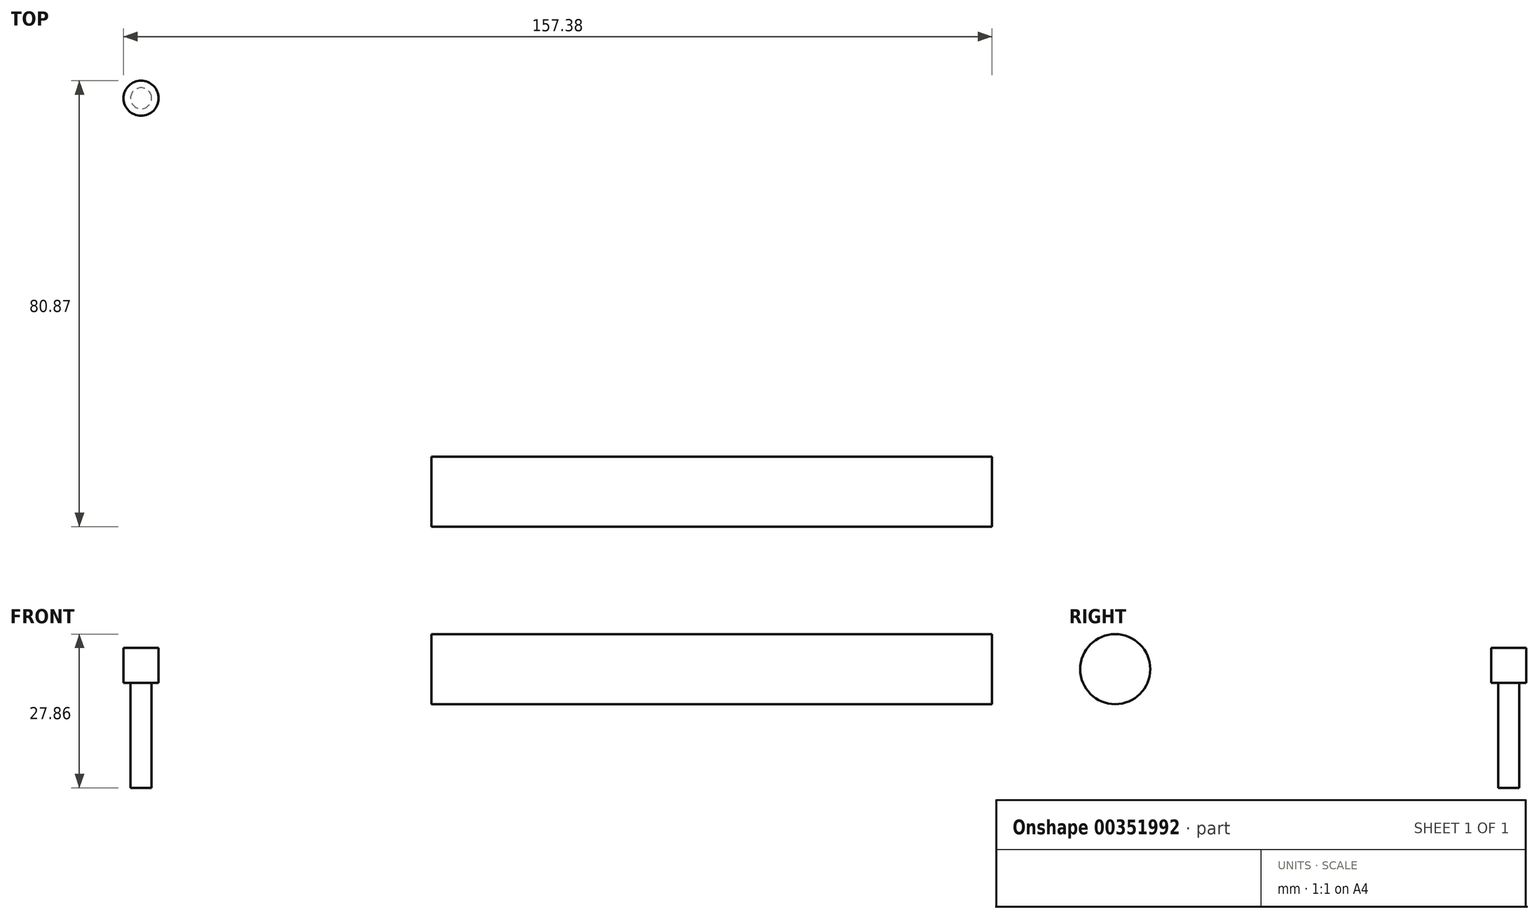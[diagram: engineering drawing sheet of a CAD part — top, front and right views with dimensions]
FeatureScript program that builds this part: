
annotation { "Feature Type Name" : "Feature", "Feature Type Description" : "" }
export const myFeature = defineFeature(function(context is Context, id is Id, definition is map)
    precondition{}
    {
        {
            var Q0;
            Q0=qCreatedBy(makeId("Right.planeOp"),FACE);
            var sketch = newSketch(context, id + "F0", { "sketchPlane" : qUnion([Q0])});
            skCircle(sketch, "E0", {"center": v(-34.98, 21.51) * mm, "radius": 6.35 * mm});
            skSolve(sketch);
        }
        {
            var Q0;
            Q0=makeQuery(id+"F0.imprint","IMPRINT",FACE,{"disambiguationData":[TD([[makeQuery(id+"F0.imprint","IMPRINT",EDGE,{"derivedFrom":sQuery(id+"F0.wireOp",EDGE,"E0")}),1.0]])]});
            extrude(context, id + "F1", {"entities" : qUnion([Q0]), "depth" : 101.6 * mm});
        }
        {
            var Q0;
            Q0=qCreatedBy(makeId("Top.planeOp"),FACE);
            var sketch = newSketch(context, id + "F2", { "sketchPlane" : qUnion([Q0])});
            skCircle(sketch, "E1", {"center": v(-52.6, 36.37) * mm, "radius": 1.9 * mm});
            skSolve(sketch);
        }
        {
            var Q0;
            Q0=makeQuery(id+"F2.imprint","IMPRINT",FACE,{"disambiguationData":[TD([[makeQuery(id+"F2.imprint","IMPRINT",EDGE,{"derivedFrom":sQuery(id+"F2.wireOp",EDGE,"E1")}),1.0]])]});
            extrude(context, id + "F3", {"entities" : qUnion([Q0]), "depth" : 19.05 * mm});
        }
        {
            var Q0;
            Q0=makeQuery(id+"F3.opExtrude","CAP_FACE",FACE,{"disambiguationData":[OSD([sQuery(id+"F2.wireOp",EDGE,"E1")])],"isStart":false});
            var sketch = newSketch(context, id + "F4", { "sketchPlane" : qUnion([Q0])});
            skCircle(sketch, "E2", {"center": v(-52.6, 36.37) * mm, "radius": 3.18 * mm});
            skSolve(sketch);
        }
        {
            var Q0;
            Q0=makeQuery(id+"F4.imprint","IMPRINT",FACE,{"disambiguationData":[TD([[makeQuery(id+"F4.imprint","IMPRINT",EDGE,{"derivedFrom":sQuery(id+"F4.wireOp",EDGE,"E2")}),1.0]])]});
            var Q1;
            Q1=makeQuery(id+"F4.imprint","IMPRINT",FACE,{"disambiguationData":[TD([[makeQuery(id+"F4.imprint","IMPRINT",EDGE,{"derivedFrom":makeQuery(id+"F3.opExtrude","CAP_EDGE",EDGE,{"disambiguationData":[OSD([sQuery(id+"F2.wireOp",EDGE,"E1")])],"isStart":false})}),1.0]])]});
            extrude(context, id + "F5", {"entities" : qUnion([Q0, Q1]), "operationType" : NewBodyOperationType.ADD, "depth" : 6.35 * mm});
        }
    });
